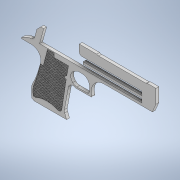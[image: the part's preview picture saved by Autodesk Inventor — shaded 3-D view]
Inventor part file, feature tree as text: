
AUTODESK INVENTOR PART (.ipt)
format: ipt  version: 2022 (Build 260153000, 153)  size: 8,051,200 bytes
history: native  units: in
note: dims shown in document units (in); Inventor stores cm internally (conversion verified against a paired STEP export)
features: sketch x8, other x8, extrude x3, reference x2, sheet_metal_op x1, plane x1, mirror x1, projected_geometry x1
ambient origin geometry x8: Origin, YZ Plane, XZ Plane, XY Plane, X Axis, Y Axis, Z Axis, Center Point
bodies: Body1 (feature_tree)
feature tree (25):
  sketch  "Sketch5"  dims[d104=0.0in]
  sketch  "Sketch3"  dims[d93=0.2333in d94=3.0666in]
  sketch  "Sketch2"  dims[d25=2.7559in d87=0.2234in]
  sheet_metal_op  "Face3"
  sketch  "Sketch8"  dims[d107=0.0079in]
  extrude  "Extrusion1"  Depth=0.2234in
  extrude  "Extrusion2"  Depth=3.0666in
  extrude  "Extrusion3"  Depth=0.0591in
  plane  "Work Plane1"
  mirror  "Mirror1"
  other  "Image2"
  other  "Image3"
  sketch  "Sketch4"  dims[d99=0.0591in d103=0.0591in]
  other  "Image4"
  other  "Plate3"
  reference  "Reference1"
  reference  "Reference2"
  sketch  "Sketch7"  dims[d105=0.0039in d106=0.0in]
  sketch  "Sketch9"  dims[d108=0.0039in d109=0.0in]
  projected_geometry  "Projected Loop1"
  sketch  "Sketch10"  dims[d110=23.622in d112=0.0197in d113=0.3937in d115=0.3937in d117=45.0deg d119=23.622in d121=0.3937in d122=0.0079in d123=0.0295in d124=135.0deg d125=0.3937in d126=0.0039in d127=0.0in]
  other  "Cut1"
  parser-record x1  (decoder bookkeeping rows leaked as tree rows — omitted from the tree; the rows remain in map.json)
  other  "Assembly1.iam"
  other  "sheetmettaal_2:2"
note: 1 file-system path scrubbed to <path> (originals preserved in map.json)
